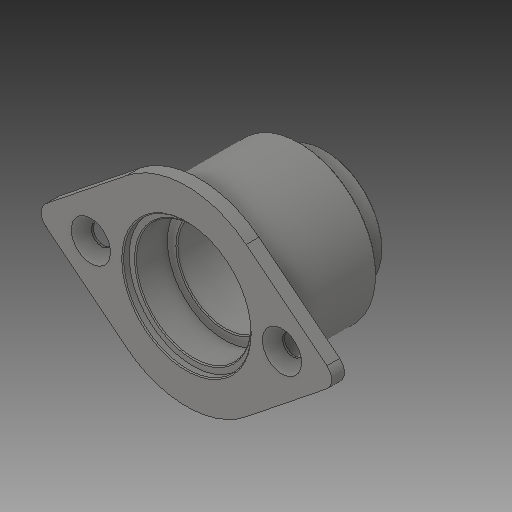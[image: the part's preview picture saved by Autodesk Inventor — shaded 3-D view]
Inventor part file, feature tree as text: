
AUTODESK INVENTOR PART (.ipt)
format: ipt  version: 2018 (Build 220112000, 112)  size: 167,936 bytes
history: native  units: in
note: dims shown in document units (in); Inventor stores cm internally (conversion verified against a paired STEP export)
features: chamfer x1
ambient origin geometry x8: Origin, YZ Plane, XZ Plane, XY Plane, X Axis, Y Axis, Z Axis, Center Point
bodies: Solid1 (feature_tree)
feature tree (1):
  chamfer  "Chamfer1"  [1 undecoded]
note: 1 required parameter value undecoded (feature->parameter linkage not recoverable at this tier; creation-order binding heuristic only, values carry confidence <= 0.55)
